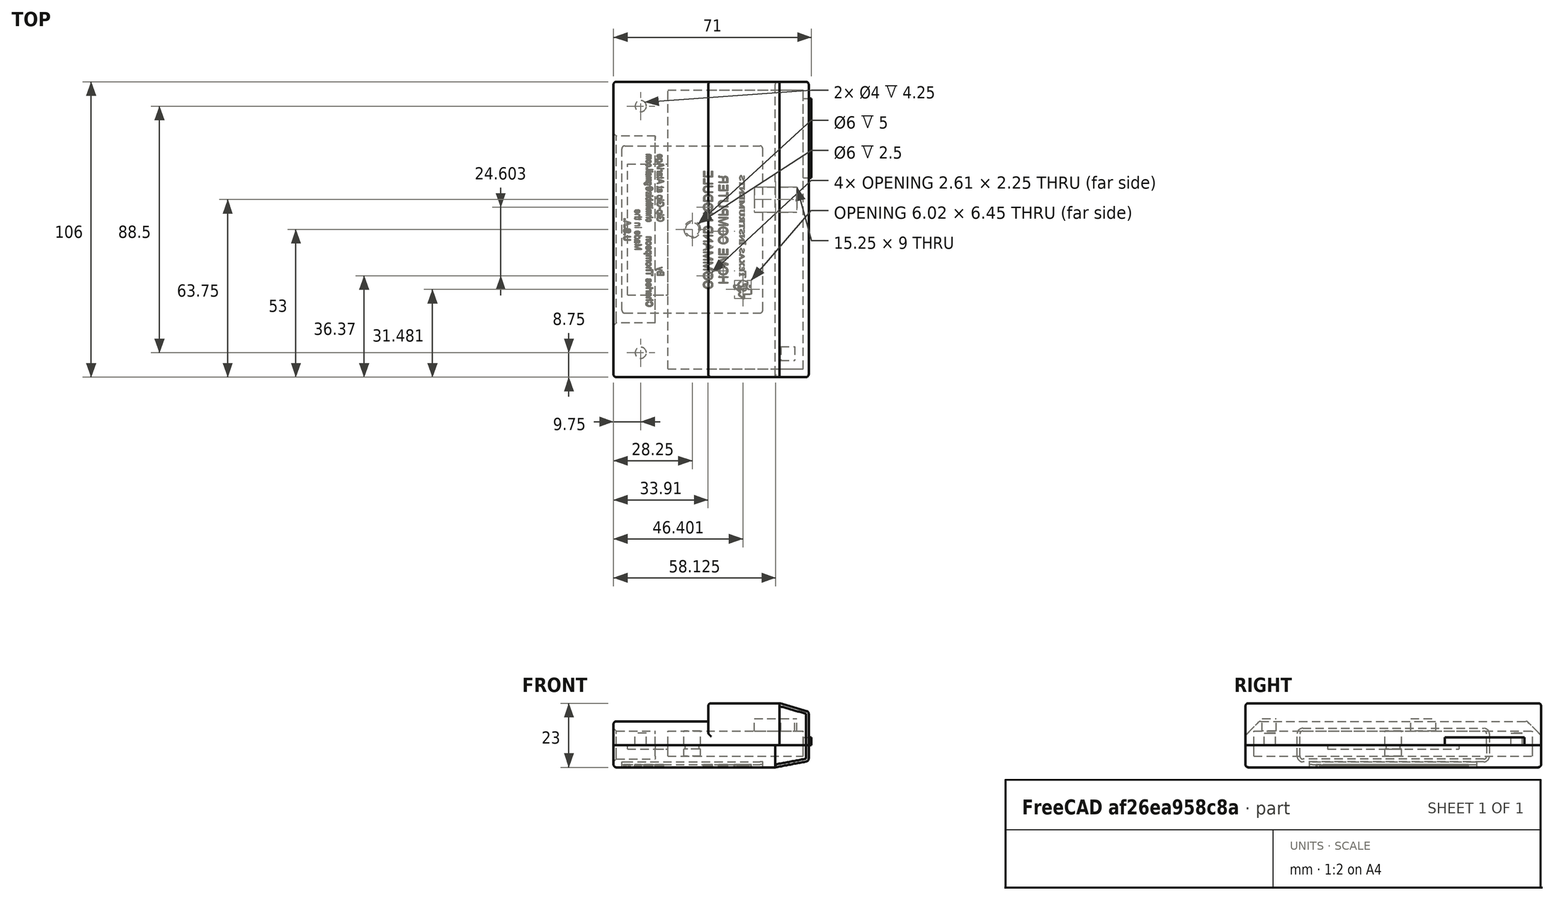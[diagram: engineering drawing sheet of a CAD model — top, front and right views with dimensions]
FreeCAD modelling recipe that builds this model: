
FCSTD DOCUMENT  (FreeCAD 0.17R11732 (Git))
Label: alcart
License: CC-BY 3.0
LicenseURL: http://creativecommons.org/licenses/by/3.0/
objects: Part::Feature×157, Part::Extrusion×119, Part::Cut×45, Part::MultiFuse×15, Part::Box×11, Part::Fillet×8, Part::Cylinder×5, Part::Chamfer×3, App::DocumentObjectGroup×3
note: 363 computed .brp shape members not serialized (recipe doc carries the construction recipe); baked Part::Feature solids carry a one-line shape summary decoded from their .brp

FEATURE [Part::Box] Box  label="fg_corepcb"
  AttacherType = Attacher::AttachEngine3D
  Height = 1.5
  Length = 48.5
  Placement = pos=(14.5,0,0) rot=(0,0,1;0rad)
  Width = 100
FEATURE [Part::Box] Box001  label="fg_connector"
  AttacherType = Attacher::AttachEngine3D
  Height = 1.5
  Length = 14.5
  Placement = pos=(0,26.5,0) rot=(0,0,1;0rad)
  Width = 47
FEATURE [Part::Box] Box002  label="fg_sdport"
  AttacherType = Attacher::AttachEngine3D
  Height = 2.75
  Length = 29
  Placement = pos=(37,68.5,1.5) rot=(0,0,1;0rad)
  Width = 28.5
FEATURE [Part::Box] Box004  label="fg_led"
  AttacherType = Attacher::AttachEngine3D
  Height = 9.5
  Length = 5
  Placement = pos=(55,3,1.5) rot=(0,0,1;0rad)
  Width = 5
FEATURE [Part::Box] Box003  label="fg_proginterface"
  AttacherType = Attacher::AttachEngine3D
  Height = 9.5
  Length = 15.25
  Placement = pos=(45.5,56.25,1.5) rot=(0,0,1;0rad)
  Width = 9
FEATURE [Part::Box] Box005  label="fg_componentarea"
  AttacherType = Attacher::AttachEngine3D
  Height = 9
  Length = 48.5
  Placement = pos=(14.5,0,-2.5) rot=(0,0,1;0rad)
  Width = 100
FEATURE [Part::Cylinder] Cylinder  label="fg_mounthole"
  Angle = 360
  AttacherType = Attacher::AttachEngine3D
  Height = 10
  Placement = pos=(23.25,50,-3) rot=(0,0,1;0rad)
  Radius = 2.5
FEATURE [Part::MultiFuse] Fusion  label="fg_mainboard"
  Shapes = -> [Box,Box005]
FEATURE [Part::Cut] Cut  label="fg_board/w/hole"
  Base = -> Fusion
  Tool = -> Cylinder
FEATURE [Part::Cylinder] Cylinder001  label="fg_mountrest1"
  Angle = 360
  AttacherType = Attacher::AttachEngine3D
  Height = 10
  Placement = pos=(23.25,50,1.5) rot=(0,0,1;0rad)
  Radius = 3
FEATURE [Part::Cut] Cut001  label="fg_board/w/rest1"
  Base = -> Cut
  Tool = -> Cylinder001
FEATURE [Part::Cylinder] Cylinder002  label="fg_mountrest2"
  Angle = 360
  AttacherType = Attacher::AttachEngine3D
  Height = 10
  Placement = pos=(23.25,50,-10) rot=(0,0,1;0rad)
  Radius = 3
FEATURE [Part::Cut] Cut002  label="fg_board/w/rest2"
  Base = -> Cut001
  Tool = -> Cylinder002
FEATURE [Part::Box] Box006  label="top_core"
  AttacherType = Attacher::AttachEngine3D
  Height = 8.5
  Length = 34
  Placement = pos=(-5,-3,1.5) rot=(0,0,1;0rad)
  Width = 106
FEATURE [Part::MultiFuse] Fusion001  label="fg_cutout1"
  Shapes = -> [Box001,Box002,Box004,Box003,Cut002]
FEATURE [Part::Box] Box007  label="top_head"
  AttacherType = Attacher::AttachEngine3D
  Height = 15
  Length = 25.5
  Placement = pos=(29,-3,1.5) rot=(0,0,1;0rad)
  Width = 106
FEATURE [Part::Chamfer] Chamfer  label="top_core_chamfer"
  Base = -> Box006
  Edges = 2 edges r=5: [Edge10,Edge12]
FEATURE [Part::MultiFuse] Fusion002
  Shapes = -> [Chamfer,Box007]
FEATURE [Part::Fillet] Fillet  label="top_fillets1"
  Base = -> Fusion002
  Edges = 5 edges r=1: [Edge7,Edge8,Edge9,Edge10,Edge13]
FEATURE [Part::Fillet] Fillet001  label="top_fillets_core&head"
  Base = -> Fillet
  Edges = 9 edges r=1: [Edge27,Edge28,Edge30,Edge31,Edge41,Edge42,Edge44,Edge45,Edge48]
FEATURE [Part::Feature] Solid  label="top_face"
  shape: bbox 10.5 x 106 x 15 mm, 6 faces (baked)
FEATURE [Part::Fillet] Fillet002  label="top_fillets_face"
  Base = -> Solid
  Edges = 5 edges r=1: [Edge8,Edge9,Edge10,Edge11,Edge12]
FEATURE [Part::MultiFuse] Fusion004  label="fg_complete"
  Shapes = -> [Box001,Box002,Box004,Box003,Cut002]
FEATURE [App::DocumentObjectGroup] Group  label="fg"
  Group = -> [Box,Box001,Box002,Box004,Box003,Box005,Cylinder,Fusion,Cut,Cylinder001,Cut001,Cut002,Fusion001,Fusion004]
FEATURE [Part::MultiFuse] Fusion003  label="top_complete"
  Shapes = -> [Fillet002,Fillet001]
FEATURE [Part::Cut] Cut003  label="top_cut1"
  Base = -> Fusion003
  Tool = -> Fusion001
FEATURE [Part::Box] Box008  label="bottom_core"
  AttacherType = Attacher::AttachEngine3D
  Height = 8
  Length = 58
  Placement = pos=(-5,-3,-6.5) rot=(0,0,1;0rad)
  Width = 106
FEATURE [Part::Feature] Solid001  label="bottom_chin"
  shape: bbox 12 x 106 x 8 mm, 6 faces (baked)
FEATURE [Part::Box] Box009  label="bottom_text_area"
  AttacherType = Attacher::AttachEngine3D
  Height = 1
  Length = 50.5
  Placement = pos=(-2,20,-6.5) rot=(0,0,1;0rad)
  Width = 60
FEATURE [Part::Fillet] Fillet003
  Base = -> Box009
  Edges = 4 edges r=1: [Edge1,Edge3,Edge5,Edge7]
FEATURE [Part::MultiFuse] Fusion005  label="bottom_w/o_fillets"
  Shapes = -> [Box008,Solid001]
FEATURE [Part::Fillet] Fillet004  label="bottom_complete"
  Base = -> Fusion005
  Edges = 10 edges r=1: [Edge1,Edge3,Edge4,Edge5,Edge10,Edge13,Edge15,Edge18,Edge19,Edge20]
FEATURE [Part::MultiFuse] Fusion006  label="fg_cutout2"
  Shapes = -> [Box001,Box002,Box004,Box003,Cut002]
FEATURE [Part::Cut] Cut004  label="bottom_cut1"
  Base = -> Fillet004
  Tool = -> Fusion006
FEATURE [Part::Box] Box010  label="Cube"
  AttacherType = Attacher::AttachEngine3D
  Height = 10
  Length = 15
  Placement = pos=(-5,16.5,-3.5) rot=(0,0,1;0rad)
  Width = 67
FEATURE [Part::Fillet] Fillet005  label="connector_cutout"
  Base = -> Box010
  Edges = 4 edges r=1: [Edge9,Edge10,Edge11,Edge12]
FEATURE [Part::Cut] Cut005  label="bottom_connector_cut"
  Base = -> Cut004
  Tool = -> Fillet005
FEATURE [Part::Fillet] Fillet006  label="connector_cutout2"
  Base = -> Box010
  Edges = 4 edges r=1: [Edge9,Edge10,Edge11,Edge12]
FEATURE [Part::Cut] Cut006  label="top_connector_cut"
  Base = -> Cut003
  Tool = -> Fillet006
FEATURE [Part::Cylinder] Cylinder003  label="index_1"
  Angle = 360
  AttacherType = Attacher::AttachEngine3D
  Height = 4.25
  Placement = pos=(0,5.75,1.5) rot=(0,0,1;0rad)
  Radius = 2
FEATURE [Part::Cylinder] Cylinder004  label="index_2"
  Angle = 360
  AttacherType = Attacher::AttachEngine3D
  Height = 4.25
  Placement = pos=(0,94.25,1.5) rot=(0,0,1;0rad)
  Radius = 2
FEATURE [Part::MultiFuse] Fusion007  label="index"
  Placement = pos=(4.75,0,0) rot=(0,0,1;0rad)
  Shapes = -> [Cylinder003,Cylinder004]
FEATURE [Part::MultiFuse] Fusion008  label="bottom_w_index"
  Shapes = -> [Cut005,Fusion007]
FEATURE [Part::MultiFuse] Fusion009  label="bottom_cutout"
  Shapes = -> [Cut005,Fusion007]
FEATURE [Part::Cut] Cut007  label="top_index_cutout"
  Base = -> Cut006
  Tool = -> Fusion009
FEATURE [Part::Feature] Face
  shape: bbox 6.877 x 6.384 x 2e-07 mm, 1 faces, 0 solids (baked)
FEATURE [Part::Feature] Face001
  shape: bbox 6.529 x 6.02 x 2e-07 mm, 1 faces, 0 solids (baked)
FEATURE [Part::Cut] Cut008
  Base = -> Face
  Tool = -> Face001
FEATURE [Part::Feature] Face002
  shape: bbox 1.264 x 2.322 x 2e-07 mm, 1 faces, 0 solids (baked)
FEATURE [Part::Feature] Face003
  shape: bbox 0.9803 x 2.192 x 2e-07 mm, 1 faces, 0 solids (baked)
FEATURE [Part::Cut] Cut009
  Base = -> Face002
  Tool = -> Face003
FEATURE [Part::Feature] Face004
  shape: bbox 0.6141 x 0.6141 x 2e-07 mm, 1 faces, 0 solids (baked)
FEATURE [Part::Feature] Face005
  shape: bbox 2.15 x 2.25 x 2.119e-07 mm, 1 faces, 0 solids (baked)
FEATURE [Part::Feature] Face006
  shape: bbox 1.67 x 1.637 x 2.385e-07 mm, 1 faces, 0 solids (baked)
FEATURE [Part::Feature] Face007
  shape: bbox 2.213 x 1.637 x 2.385e-07 mm, 1 faces, 0 solids (baked)
FEATURE [Part::Feature] Face008
  shape: bbox 2.213 x 1.711 x 2.385e-07 mm, 1 faces, 0 solids (baked)
FEATURE [Part::Feature] Face009
  shape: bbox 0.641 x 0.6678 x 2.385e-07 mm, 1 faces, 0 solids (baked)
FEATURE [Part::Cut] Cut010
  Base = -> Face008
  Tool = -> Face009
FEATURE [Part::Feature] Face010
  shape: bbox 1.419 x 1.715 x 2.385e-07 mm, 1 faces, 0 solids (baked)
FEATURE [Part::Feature] Face011
  shape: bbox 0.75 x 2.25 x 2.07e-07 mm, 1 faces, 0 solids (baked)
FEATURE [Part::Feature] Face012
  shape: bbox 2.382 x 1.71 x 2.417e-07 mm, 1 faces, 0 solids (baked)
FEATURE [Part::Feature] Face013
  shape: bbox 1.487 x 1.75 x 2.417e-07 mm, 1 faces, 0 solids (baked)
FEATURE [Part::Feature] Face014
  shape: bbox 2.078 x 1.671 x 2.417e-07 mm, 1 faces, 0 solids (baked)
FEATURE [Part::Feature] Face015
  shape: bbox 0.8461 x 0.693 x 2.417e-07 mm, 1 faces, 0 solids (baked)
FEATURE [Part::Feature] Face016
  shape: bbox 2.126 x 1.729 x 2.417e-07 mm, 1 faces, 0 solids (baked)
FEATURE [Part::Cut] Cut011
  Base = -> Face016
  Tool = -> Face015
FEATURE [Part::Feature] Face017
  shape: bbox 2.372 x 1.71 x 2.417e-07 mm, 1 faces, 0 solids (baked)
FEATURE [Part::Feature] Face018
  shape: bbox 2.924 x 1.67 x 2.417e-07 mm, 1 faces, 0 solids (baked)
FEATURE [Part::Feature] Face019
  shape: bbox 1.75 x 1.67 x 2.417e-07 mm, 1 faces, 0 solids (baked)
FEATURE [Part::Feature] Face020
  shape: bbox 2.382 x 1.71 x 2.417e-07 mm, 1 faces, 0 solids (baked)
FEATURE [Part::Feature] Face021
  shape: bbox 2.078 x 1.671 x 2.417e-07 mm, 1 faces, 0 solids (baked)
FEATURE [Part::Feature] Face022
  shape: bbox 1.487 x 1.75 x 2.417e-07 mm, 1 faces, 0 solids (baked)
FEATURE [Part::Extrusion] Extrude
  Base = -> Cut008
  Dir = (0,0,-1)
  DirMode = 2
  FaceMakerClass = Part::FaceMakerBullseye
  LengthFwd = 1
  LengthRev = 0
  Solid = false
  Symmetric = false
FEATURE [Part::Extrusion] Extrude001
  Base = -> Cut009
  Dir = (0,0,-1)
  DirMode = 2
  FaceMakerClass = Part::FaceMakerBullseye
  LengthFwd = 1
  LengthRev = 0
  Solid = false
  Symmetric = false
FEATURE [Part::Extrusion] Extrude002
  Base = -> Face004
  Dir = (0,0,1)
  DirMode = 2
  FaceMakerClass = Part::FaceMakerBullseye
  LengthFwd = -1
  LengthRev = 0
  Solid = false
  Symmetric = false
FEATURE [Part::Extrusion] Extrude003
  Base = -> Face005
  Dir = (0,0,1)
  DirMode = 2
  FaceMakerClass = Part::FaceMakerBullseye
  LengthFwd = -1
  LengthRev = 0
  Solid = false
  Symmetric = false
FEATURE [Part::Extrusion] Extrude004
  Base = -> Face006
  Dir = (0,0,1)
  DirMode = 2
  FaceMakerClass = Part::FaceMakerBullseye
  LengthFwd = -1
  LengthRev = 0
  Solid = false
  Symmetric = false
FEATURE [Part::Extrusion] Extrude005
  Base = -> Face007
  Dir = (0,0,1)
  DirMode = 2
  FaceMakerClass = Part::FaceMakerBullseye
  LengthFwd = -1
  LengthRev = 0
  Solid = false
  Symmetric = false
FEATURE [Part::Extrusion] Extrude006
  Base = -> Cut010
  Dir = (0,0,1)
  DirMode = 2
  FaceMakerClass = Part::FaceMakerBullseye
  LengthFwd = -1
  LengthRev = 0
  Solid = false
  Symmetric = false
FEATURE [Part::Extrusion] Extrude007
  Base = -> Face010
  Dir = (0,0,1)
  DirMode = 2
  FaceMakerClass = Part::FaceMakerBullseye
  LengthFwd = -1
  LengthRev = 0
  Solid = false
  Symmetric = false
FEATURE [Part::Extrusion] Extrude008
  Base = -> Face011
  Dir = (0,0,1)
  DirMode = 2
  FaceMakerClass = Part::FaceMakerBullseye
  LengthFwd = -1
  LengthRev = 0
  Solid = false
  Symmetric = false
FEATURE [Part::Extrusion] Extrude009
  Base = -> Face012
  Dir = (0,0,1)
  DirMode = 2
  FaceMakerClass = Part::FaceMakerBullseye
  LengthFwd = -1
  LengthRev = 0
  Solid = false
  Symmetric = false
FEATURE [Part::Extrusion] Extrude010
  Base = -> Face013
  Dir = (0,0,1)
  DirMode = 2
  FaceMakerClass = Part::FaceMakerBullseye
  LengthFwd = -1
  LengthRev = 0
  Solid = false
  Symmetric = false
FEATURE [Part::Extrusion] Extrude011
  Base = -> Face014
  Dir = (0,0,1)
  DirMode = 2
  FaceMakerClass = Part::FaceMakerBullseye
  LengthFwd = -1
  LengthRev = 0
  Solid = false
  Symmetric = false
FEATURE [Part::Extrusion] Extrude012
  Base = -> Cut011
  Dir = (0,0,1)
  DirMode = 2
  FaceMakerClass = Part::FaceMakerBullseye
  LengthFwd = -1
  LengthRev = 0
  Solid = false
  Symmetric = false
FEATURE [Part::Extrusion] Extrude013
  Base = -> Face017
  Dir = (0,0,-1)
  DirMode = 2
  FaceMakerClass = Part::FaceMakerBullseye
  LengthFwd = 1
  LengthRev = 0
  Solid = false
  Symmetric = false
FEATURE [Part::Extrusion] Extrude014
  Base = -> Face018
  Dir = (0,0,-1)
  DirMode = 2
  FaceMakerClass = Part::FaceMakerBullseye
  LengthFwd = 1
  LengthRev = 0
  Solid = false
  Symmetric = false
FEATURE [Part::Extrusion] Extrude015
  Base = -> Face019
  Dir = (0,0,1)
  DirMode = 2
  FaceMakerClass = Part::FaceMakerBullseye
  LengthFwd = -1
  LengthRev = 0
  Solid = false
  Symmetric = false
FEATURE [Part::Extrusion] Extrude016
  Base = -> Face020
  Dir = (0,0,1)
  DirMode = 2
  FaceMakerClass = Part::FaceMakerBullseye
  LengthFwd = -1
  LengthRev = 0
  Solid = false
  Symmetric = false
FEATURE [Part::Extrusion] Extrude017
  Base = -> Face021
  Dir = (0,0,1)
  DirMode = 2
  FaceMakerClass = Part::FaceMakerBullseye
  LengthFwd = -1
  LengthRev = 0
  Solid = false
  Symmetric = false
FEATURE [Part::Extrusion] Extrude018
  Base = -> Face022
  Dir = (0,0,1)
  DirMode = 2
  FaceMakerClass = Part::FaceMakerBullseye
  LengthFwd = -1
  LengthRev = 0
  Solid = false
  Symmetric = false
FEATURE [Part::MultiFuse] Fusion010  label="texas_instruments"
  Placement = pos=(44.5,25,-6.5) rot=(0.707107,0.707107,0;3.14159rad)
  Shapes = -> [Extrude018,Extrude,Extrude002,Extrude006,Extrude003,Extrude001,Extrude004,Extrude005,Extrude007,Extrude009,Extrude008,Extrude010,Extrude014,Extrude012,Extrude011,Extrude015,Extrude013,Extrude017,Extrude016]
FEATURE [Part::Cut] Cut012  label="bottom_w_textbox"
  Base = -> Fusion008
  Tool = -> Fillet003
FEATURE [Part::Feature] Face023
  shape: bbox 2.434 x 3.167 x 2.001e-07 mm, 1 faces, 0 solids (baked)
FEATURE [Part::Feature] Face024
  shape: bbox 3.055 x 3.319 x 2.001e-07 mm, 1 faces, 0 solids (baked)
FEATURE [Part::Feature] Face025
  shape: bbox 2.248 x 2.607 x 2.001e-07 mm, 1 faces, 0 solids (baked)
FEATURE [Part::Cut] Cut013
  Base = -> Face024
  Tool = -> Face025
FEATURE [Part::Feature] Face026
  shape: bbox 2.977 x 3.167 x 2.001e-07 mm, 1 faces, 0 solids (baked)
FEATURE [Part::Feature] Face027
  shape: bbox 2.269 x 3.167 x 2.001e-07 mm, 1 faces, 0 solids (baked)
FEATURE [Part::Feature] Face028
  shape: bbox 2.729 x 3.319 x 2.001e-07 mm, 1 faces, 0 solids (baked)
FEATURE [Part::Feature] Face029
  shape: bbox 3.055 x 3.319 x 2.001e-07 mm, 1 faces, 0 solids (baked)
FEATURE [Part::Feature] Face030
  shape: bbox 2.248 x 2.607 x 2.001e-07 mm, 1 faces, 0 solids (baked)
FEATURE [Part::Cut] Cut014
  Base = -> Face029
  Tool = -> Face030
FEATURE [Part::Feature] Face031
  shape: bbox 2.977 x 3.167 x 2.001e-07 mm, 1 faces, 0 solids (baked)
FEATURE [Part::Feature] Face032
  shape: bbox 2.282 x 3.167 x 2.001e-07 mm, 1 faces, 0 solids (baked)
FEATURE [Part::Feature] Face033
  shape: bbox 1.458 x 1.112 x 2.001e-07 mm, 1 faces, 0 solids (baked)
FEATURE [Part::Cut] Cut015
  Base = -> Face032
  Tool = -> Face033
FEATURE [Part::Feature] Face034
  shape: bbox 2.43 x 3.267 x 2.001e-07 mm, 1 faces, 0 solids (baked)
FEATURE [Part::Feature] Face035
  shape: bbox 2.482 x 3.167 x 2.001e-07 mm, 1 faces, 0 solids (baked)
FEATURE [Part::Feature] Face036
  shape: bbox 2.269 x 3.167 x 2.001e-07 mm, 1 faces, 0 solids (baked)
FEATURE [Part::Feature] Face037
  shape: bbox 2.543 x 3.167 x 2.001e-07 mm, 1 faces, 0 solids (baked)
FEATURE [Part::Feature] Face038
  shape: bbox 1.597 x 1.09 x 2.001e-07 mm, 1 faces, 0 solids (baked)
FEATURE [Part::Cut] Cut016
  Base = -> Face037
  Tool = -> Face038
FEATURE [Part::Feature] Face039
  shape: bbox 2.729 x 3.319 x 2.001e-07 mm, 1 faces, 0 solids (baked)
FEATURE [Part::Feature] Face040
  shape: bbox 3.055 x 3.319 x 2.001e-07 mm, 1 faces, 0 solids (baked)
FEATURE [Part::Feature] Face041
  shape: bbox 2.248 x 2.607 x 2.001e-07 mm, 1 faces, 0 solids (baked)
FEATURE [Part::Cut] Cut017
  Base = -> Face040
  Tool = -> Face041
FEATURE [Part::Feature] Face042
  shape: bbox 2.977 x 3.167 x 2.001e-07 mm, 1 faces, 0 solids (baked)
FEATURE [Part::Feature] Face043
  shape: bbox 2.977 x 3.167 x 2.001e-07 mm, 1 faces, 0 solids (baked)
FEATURE [Part::Feature] Face044
  shape: bbox 1.007 x 1.442 x 2.001e-07 mm, 1 faces, 0 solids (baked)
FEATURE [Part::Feature] Face045
  shape: bbox 2.76 x 3.167 x 2.001e-07 mm, 1 faces, 0 solids (baked)
FEATURE [Part::Cut] Cut018
  Base = -> Face045
  Tool = -> Face044
FEATURE [Part::Feature] Face046
  shape: bbox 2.473 x 3.167 x 2.001e-07 mm, 1 faces, 0 solids (baked)
FEATURE [Part::Feature] Face047
  shape: bbox 2.508 x 3.167 x 2.001e-07 mm, 1 faces, 0 solids (baked)
FEATURE [Part::Feature] Face048
  shape: bbox 1.701 x 2.455 x 2.001e-07 mm, 1 faces, 0 solids (baked)
FEATURE [Part::Cut] Cut019
  Base = -> Face047
  Tool = -> Face048
FEATURE [Part::Feature] Face049
  shape: bbox 2.977 x 3.167 x 2.001e-07 mm, 1 faces, 0 solids (baked)
FEATURE [Part::Feature] Face050
  shape: bbox 3.055 x 3.319 x 2.001e-07 mm, 1 faces, 0 solids (baked)
FEATURE [Part::Feature] Face051
  shape: bbox 2.248 x 2.607 x 2.001e-07 mm, 1 faces, 0 solids (baked)
FEATURE [Part::Cut] Cut020
  Base = -> Face050
  Tool = -> Face051
FEATURE [Part::Feature] Face052
  shape: bbox 2.508 x 3.167 x 2.001e-07 mm, 1 faces, 0 solids (baked)
FEATURE [Part::Feature] Face053
  shape: bbox 1.701 x 2.455 x 2.001e-07 mm, 1 faces, 0 solids (baked)
FEATURE [Part::Cut] Cut021
  Base = -> Face052
  Tool = -> Face053
FEATURE [Part::Feature] Face054
  shape: bbox 2.43 x 3.267 x 2.001e-07 mm, 1 faces, 0 solids (baked)
FEATURE [Part::Feature] Face055
  shape: bbox 1.966 x 3.167 x 2.001e-07 mm, 1 faces, 0 solids (baked)
FEATURE [Part::Feature] Face056
  shape: bbox 2.269 x 3.167 x 2.001e-07 mm, 1 faces, 0 solids (baked)
FEATURE [Part::Extrusion] Extrude019
  Base = -> Face023
  Dir = (0,0,-1)
  DirMode = 2
  FaceMakerClass = Part::FaceMakerBullseye
  LengthFwd = 1
  LengthRev = 0
  Solid = true
  Symmetric = false
FEATURE [Part::Extrusion] Extrude020
  Base = -> Cut013
  Dir = (0,0,-1)
  DirMode = 2
  FaceMakerClass = Part::FaceMakerBullseye
  LengthFwd = 1
  LengthRev = 0
  Solid = true
  Symmetric = false
FEATURE [Part::Extrusion] Extrude021
  Base = -> Face026
  Dir = (0,0,1)
  DirMode = 2
  FaceMakerClass = Part::FaceMakerBullseye
  LengthFwd = -1
  LengthRev = 0
  Solid = true
  Symmetric = false
FEATURE [Part::Extrusion] Extrude022
  Base = -> Face027
  Dir = (0,0,-1)
  DirMode = 2
  FaceMakerClass = Part::FaceMakerBullseye
  LengthFwd = 1
  LengthRev = 0
  Solid = true
  Symmetric = false
FEATURE [Part::Extrusion] Extrude023
  Base = -> Face028
  Dir = (0,0,-1)
  DirMode = 2
  FaceMakerClass = Part::FaceMakerBullseye
  LengthFwd = 1
  LengthRev = 0
  Solid = true
  Symmetric = false
FEATURE [Part::Extrusion] Extrude024
  Base = -> Cut014
  Dir = (0,0,-1)
  DirMode = 2
  FaceMakerClass = Part::FaceMakerBullseye
  LengthFwd = 1
  LengthRev = 0
  Solid = true
  Symmetric = false
FEATURE [Part::Extrusion] Extrude025
  Base = -> Face031
  Dir = (0,0,1)
  DirMode = 2
  FaceMakerClass = Part::FaceMakerBullseye
  LengthFwd = -1
  LengthRev = 0
  Solid = true
  Symmetric = false
FEATURE [Part::Extrusion] Extrude026
  Base = -> Cut015
  Dir = (0,0,-1)
  DirMode = 2
  FaceMakerClass = Part::FaceMakerBullseye
  LengthFwd = 1
  LengthRev = 0
  Solid = true
  Symmetric = false
FEATURE [Part::Extrusion] Extrude027
  Base = -> Face034
  Dir = (0,0,1)
  DirMode = 2
  FaceMakerClass = Part::FaceMakerBullseye
  LengthFwd = -1
  LengthRev = 0
  Solid = true
  Symmetric = false
FEATURE [Part::Extrusion] Extrude028
  Base = -> Face035
  Dir = (0,0,-1)
  DirMode = 2
  FaceMakerClass = Part::FaceMakerBullseye
  LengthFwd = 1
  LengthRev = 0
  Solid = true
  Symmetric = false
FEATURE [Part::Extrusion] Extrude029
  Base = -> Face036
  Dir = (0,0,-1)
  DirMode = 2
  FaceMakerClass = Part::FaceMakerBullseye
  LengthFwd = 1
  LengthRev = 0
  Solid = true
  Symmetric = false
FEATURE [Part::Extrusion] Extrude030
  Base = -> Cut016
  Dir = (0,0,1)
  DirMode = 2
  FaceMakerClass = Part::FaceMakerBullseye
  LengthFwd = -1
  LengthRev = 0
  Solid = true
  Symmetric = false
FEATURE [Part::Extrusion] Extrude031
  Base = -> Face039
  Dir = (0,0,-1)
  DirMode = 2
  FaceMakerClass = Part::FaceMakerBullseye
  LengthFwd = 1
  LengthRev = 0
  Solid = true
  Symmetric = false
FEATURE [Part::Extrusion] Extrude032
  Base = -> Cut017
  Dir = (0,0,-1)
  DirMode = 2
  FaceMakerClass = Part::FaceMakerBullseye
  LengthFwd = 1
  LengthRev = 0
  Solid = true
  Symmetric = false
FEATURE [Part::Extrusion] Extrude033
  Base = -> Face042
  Dir = (0,0,1)
  DirMode = 2
  FaceMakerClass = Part::FaceMakerBullseye
  LengthFwd = -1
  LengthRev = 0
  Solid = true
  Symmetric = false
FEATURE [Part::Extrusion] Extrude034
  Base = -> Face043
  Dir = (0,0,1)
  DirMode = 2
  FaceMakerClass = Part::FaceMakerBullseye
  LengthFwd = -1
  LengthRev = 0
  Solid = true
  Symmetric = false
FEATURE [Part::Extrusion] Extrude035
  Base = -> Cut018
  Dir = (0,0,-1)
  DirMode = 2
  FaceMakerClass = Part::FaceMakerBullseye
  LengthFwd = 1
  LengthRev = 0
  Solid = true
  Symmetric = false
FEATURE [Part::Extrusion] Extrude036
  Base = -> Face046
  Dir = (0,0,-1)
  DirMode = 2
  FaceMakerClass = Part::FaceMakerBullseye
  LengthFwd = 1
  LengthRev = 0
  Solid = true
  Symmetric = false
FEATURE [Part::Extrusion] Extrude037
  Base = -> Cut019
  Dir = (0,0,-1)
  DirMode = 2
  FaceMakerClass = Part::FaceMakerBullseye
  LengthFwd = 1
  LengthRev = 0
  Solid = true
  Symmetric = false
FEATURE [Part::Extrusion] Extrude038
  Base = -> Face049
  Dir = (0,0,1)
  DirMode = 2
  FaceMakerClass = Part::FaceMakerBullseye
  LengthFwd = -1
  LengthRev = 0
  Solid = true
  Symmetric = false
FEATURE [Part::Extrusion] Extrude039
  Base = -> Cut020
  Dir = (0,0,-1)
  DirMode = 2
  FaceMakerClass = Part::FaceMakerBullseye
  LengthFwd = 1
  LengthRev = 0
  Solid = true
  Symmetric = false
FEATURE [Part::Extrusion] Extrude040
  Base = -> Cut021
  Dir = (0,0,-1)
  DirMode = 2
  FaceMakerClass = Part::FaceMakerBullseye
  LengthFwd = 1
  LengthRev = 0
  Solid = true
  Symmetric = false
FEATURE [Part::Extrusion] Extrude041
  Base = -> Face054
  Dir = (0,0,1)
  DirMode = 2
  FaceMakerClass = Part::FaceMakerBullseye
  LengthFwd = -1
  LengthRev = 0
  Solid = true
  Symmetric = false
FEATURE [Part::Extrusion] Extrude042
  Base = -> Face056
  Dir = (0,0,-1)
  DirMode = 2
  FaceMakerClass = Part::FaceMakerBullseye
  LengthFwd = 1
  LengthRev = 0
  Solid = true
  Symmetric = false
FEATURE [Part::Extrusion] Extrude043
  Base = -> Face055
  Dir = (0,0,-1)
  DirMode = 2
  FaceMakerClass = Part::FaceMakerBullseye
  LengthFwd = 1
  LengthRev = 0
  Solid = true
  Symmetric = false
FEATURE [Part::MultiFuse] Fusion011  label="command_module"
  Placement = pos=(36,28.75,-6.5) rot=(0.707107,0.707107,0;3.14159rad)
  Shapes = -> [Extrude031,Extrude019,Extrude020,Extrude021,Extrude022,Extrude037,Extrude023,Extrude025,Extrude024,Extrude026,Extrude027,Extrude028,Extrude032,Extrude034,Extrude029,Extrude030,Extrude033,Extrude035,Extrude036,Extrude038,Extrude039,Extrude040,Extrude041,Extrude042,Extrude043]
FEATURE [Part::Feature] Face057
  shape: bbox 1.929 x 2.309 x 2e-07 mm, 1 faces, 0 solids (baked)
FEATURE [Part::Feature] Face058
  shape: bbox 1.386 x 1.78 x 2e-07 mm, 1 faces, 0 solids (baked)
FEATURE [Part::Feature] Face059
  shape: bbox 0.731 x 0.6621 x 2e-07 mm, 1 faces, 0 solids (baked)
FEATURE [Part::Cut] Cut022
  Base = -> Face058
  Tool = -> Face059
FEATURE [Part::Feature] Face060
  shape: bbox 1.319 x 2.382 x 2e-07 mm, 1 faces, 0 solids (baked)
FEATURE [Part::Feature] Face061
  shape: bbox 0.8407 x 1.286 x 2e-07 mm, 1 faces, 0 solids (baked)
FEATURE [Part::Cut] Cut023
  Base = -> Face060
  Tool = -> Face061
FEATURE [Part::Feature] Face062
  shape: bbox 1.33 x 1.78 x 2e-07 mm, 1 faces, 0 solids (baked)
FEATURE [Part::Feature] Face063
  shape: bbox 0.8295 x 0.5069 x 2e-07 mm, 1 faces, 0 solids (baked)
FEATURE [Part::Cut] Cut024
  Base = -> Face062
  Tool = -> Face063
FEATURE [Part::Feature] Face064
  shape: bbox 0.2334 x 1.66 x 2e-07 mm, 1 faces, 0 solids (baked)
FEATURE [Part::Feature] Face065
  shape: bbox 0.2362 x 0.3326 x 2e-07 mm, 1 faces, 0 solids (baked)
FEATURE [Part::Feature] Face066
  shape: bbox 1.172 x 1.707 x 2e-07 mm, 1 faces, 0 solids (baked)
FEATURE [Part::Feature] Face067
  shape: bbox 0.6748 x 2.189 x 2e-07 mm, 1 faces, 0 solids (baked)
FEATURE [Part::Feature] Face068
  shape: bbox 1.17 x 2.309 x 2e-07 mm, 1 faces, 0 solids (baked)
FEATURE [Part::Feature] Face069
  shape: bbox 1.33 x 1.78 x 2e-07 mm, 1 faces, 0 solids (baked)
FEATURE [Part::Feature] Face070
  shape: bbox 0.8295 x 0.5069 x 2e-07 mm, 1 faces, 0 solids (baked)
FEATURE [Part::Cut] Cut025
  Base = -> Face069
  Tool = -> Face070
FEATURE [Part::Feature] Face071
  shape: bbox 1.625 x 2.382 x 2e-07 mm, 1 faces, 0 solids (baked)
FEATURE [Part::Feature] Face072
  shape: bbox 0.4218 x 0.4625 x 2e-07 mm, 1 faces, 0 solids (baked)
FEATURE [Part::Feature] Face073
  shape: bbox 1.69 x 2.42 x 2e-07 mm, 1 faces, 0 solids (baked)
FEATURE [Part::Feature] Face074
  shape: bbox 0.4218 x 0.4625 x 2e-07 mm, 1 faces, 0 solids (baked)
FEATURE [Part::Feature] Face075
  shape: bbox 1.904 x 2.309 x 2e-07 mm, 1 faces, 0 solids (baked)
FEATURE [Part::Feature] Face076
  shape: bbox 0.5342 x 0.9029 x 2e-07 mm, 1 faces, 0 solids (baked)
FEATURE [Part::Cut] Cut026
  Base = -> Face075
  Tool = -> Face076
FEATURE [Part::Feature] Face077
  shape: bbox 0.4218 x 0.4625 x 2e-07 mm, 1 faces, 0 solids (baked)
FEATURE [Part::Extrusion] Extrude044
  Base = -> Face057
  Dir = (0,0,1)
  DirMode = 2
  FaceMakerClass = Part::FaceMakerBullseye
  LengthFwd = -1
  LengthRev = 0
  Solid = true
  Symmetric = false
FEATURE [Part::Extrusion] Extrude045
  Base = -> Cut022
  Dir = (0,0,1)
  DirMode = 2
  FaceMakerClass = Part::FaceMakerBullseye
  LengthFwd = -1
  LengthRev = 0
  Solid = true
  Symmetric = false
FEATURE [Part::Extrusion] Extrude046
  Base = -> Cut023
  Dir = (0,0,-1)
  DirMode = 2
  FaceMakerClass = Part::FaceMakerBullseye
  LengthFwd = 1
  LengthRev = 0
  Solid = true
  Symmetric = false
FEATURE [Part::Extrusion] Extrude047
  Base = -> Cut024
  Dir = (0,0,-1)
  DirMode = 2
  FaceMakerClass = Part::FaceMakerBullseye
  LengthFwd = 1
  LengthRev = 0
  Solid = true
  Symmetric = false
FEATURE [Part::Extrusion] Extrude048
  Base = -> Face064
  Dir = (0,0,-1)
  DirMode = 2
  FaceMakerClass = Part::FaceMakerBullseye
  LengthFwd = 1
  LengthRev = 0
  Solid = true
  Symmetric = false
FEATURE [Part::Extrusion] Extrude049
  Base = -> Face065
  Dir = (0,0,-1)
  DirMode = 2
  FaceMakerClass = Part::FaceMakerBullseye
  LengthFwd = 1
  LengthRev = 0
  Solid = true
  Symmetric = false
FEATURE [Part::Extrusion] Extrude050
  Base = -> Face066
  Dir = (0,0,-1)
  DirMode = 2
  FaceMakerClass = Part::FaceMakerBullseye
  LengthFwd = 1
  LengthRev = 0
  Solid = true
  Symmetric = false
FEATURE [Part::Extrusion] Extrude051
  Base = -> Face067
  Dir = (0,0,1)
  DirMode = 2
  FaceMakerClass = Part::FaceMakerBullseye
  LengthFwd = -1
  LengthRev = 0
  Solid = true
  Symmetric = false
FEATURE [Part::Extrusion] Extrude052
  Base = -> Face068
  Dir = (0,0,-1)
  DirMode = 2
  FaceMakerClass = Part::FaceMakerBullseye
  LengthFwd = 1
  LengthRev = 0
  Solid = true
  Symmetric = false
FEATURE [Part::Extrusion] Extrude053
  Base = -> Cut025
  Dir = (0,0,-1)
  DirMode = 2
  FaceMakerClass = Part::FaceMakerBullseye
  LengthFwd = 1
  LengthRev = 0
  Solid = true
  Symmetric = false
FEATURE [Part::Extrusion] Extrude054
  Base = -> Face071
  Dir = (0,0,1)
  DirMode = 2
  FaceMakerClass = Part::FaceMakerBullseye
  LengthFwd = -1
  LengthRev = 0
  Solid = true
  Symmetric = false
FEATURE [Part::Extrusion] Extrude055
  Base = -> Face072
  Dir = (0,0,-1)
  DirMode = 2
  FaceMakerClass = Part::FaceMakerBullseye
  LengthFwd = 1
  LengthRev = 0
  Solid = true
  Symmetric = false
FEATURE [Part::Extrusion] Extrude056
  Base = -> Face074
  Dir = (0,0,-1)
  DirMode = 2
  FaceMakerClass = Part::FaceMakerBullseye
  LengthFwd = 1
  LengthRev = 0
  Solid = true
  Symmetric = false
FEATURE [Part::Extrusion] Extrude057
  Base = -> Face073
  Dir = (0,0,-1)
  DirMode = 2
  FaceMakerClass = Part::FaceMakerBullseye
  LengthFwd = 1
  LengthRev = 0
  Solid = true
  Symmetric = false
FEATURE [Part::Extrusion] Extrude058
  Base = -> Cut026
  Dir = (0,0,-1)
  DirMode = 2
  FaceMakerClass = Part::FaceMakerBullseye
  LengthFwd = 1
  LengthRev = 0
  Solid = true
  Symmetric = false
FEATURE [Part::Extrusion] Extrude059
  Base = -> Face077
  Dir = (0,0,-1)
  DirMode = 2
  FaceMakerClass = Part::FaceMakerBullseye
  LengthFwd = 1
  LengthRev = 0
  Solid = true
  Symmetric = false
FEATURE [Part::MultiFuse] Fusion012  label="origin"
  Placement = pos=(5,37,-6.5) rot=(0.707107,0.707107,0;3.14159rad)
  Shapes = -> [Extrude059,Extrude056,Extrude058,Extrude057,Extrude053,Extrude055,Extrude052,Extrude054,Extrude050,Extrude051,Extrude048,Extrude046,Extrude049,Extrude047,Extrude045,Extrude044]
FEATURE [Part::Feature] Subtraction
  shape: bbox 1.53 x 2.309 x 2e-07 mm, 1 faces, 0 solids (baked)
FEATURE [Part::Feature] Face078
  shape: bbox 1.288 x 2.351 x 2e-07 mm, 1 faces, 0 solids (baked)
FEATURE [Part::Feature] Face079
  shape: bbox 1.802 x 2.42 x 2e-07 mm, 1 faces, 0 solids (baked)
FEATURE [Part::Feature] Face080
  shape: bbox 1.333 x 2.309 x 2e-07 mm, 1 faces, 0 solids (baked)
FEATURE [Part::Feature] Face081
  shape: bbox 1.395 x 1.812 x 2e-07 mm, 1 faces, 0 solids (baked)
FEATURE [Part::Feature] Face082
  shape: bbox 0.5258 x 0.5227 x 2e-07 mm, 1 faces, 0 solids (baked)
FEATURE [Part::Cut] Cut027
  Base = -> Face081
  Tool = -> Face082
FEATURE [Part::Feature] Face083
  shape: bbox 0.8632 x 1.739 x 2e-07 mm, 1 faces, 0 solids (baked)
FEATURE [Part::Feature] Face084
  shape: bbox 0.3936 x 2.309 x 2e-07 mm, 1 faces, 0 solids (baked)
FEATURE [Part::Feature] Face085
  shape: bbox 1.414 x 1.812 x 2e-07 mm, 1 faces, 0 solids (baked)
FEATURE [Part::Feature] Face086
  shape: bbox 0.6045 x 0.3897 x 2e-07 mm, 1 faces, 0 solids (baked)
FEATURE [Part::Cut] Cut028
  Base = -> Face085
  Tool = -> Face086
FEATURE [Part::Feature] Face087
  shape: bbox 1.381 x 1.812 x 2e-07 mm, 1 faces, 0 solids (baked)
FEATURE [Part::Feature] Face088
  shape: bbox 1.642 x 2.309 x 2e-07 mm, 1 faces, 0 solids (baked)
FEATURE [Part::Feature] Face089
  shape: bbox 1.333 x 2.309 x 2e-07 mm, 1 faces, 0 solids (baked)
FEATURE [Part::Feature] Face090
  shape: bbox 1.501 x 1.812 x 2e-07 mm, 1 faces, 0 solids (baked)
FEATURE [Part::Feature] Face091
  shape: bbox 0.7142 x 1.096 x 2e-07 mm, 1 faces, 0 solids (baked)
FEATURE [Part::Cut] Cut029
  Base = -> Face090
  Tool = -> Face091
FEATURE [Part::Feature] Face092
  shape: bbox 2.148 x 1.739 x 2e-07 mm, 1 faces, 0 solids (baked)
FEATURE [Part::Feature] Face093
  shape: bbox 1.451 x 2.43 x 2e-07 mm, 1 faces, 0 solids (baked)
FEATURE [Part::Feature] Face094
  shape: bbox 0.6636 x 1.074 x 2e-07 mm, 1 faces, 0 solids (baked)
FEATURE [Part::Cut] Cut030
  Base = -> Face093
  Tool = -> Face094
FEATURE [Part::Feature] Face095
  shape: bbox 1.381 x 1.812 x 2e-07 mm, 1 faces, 0 solids (baked)
FEATURE [Part::Feature] Face096
  shape: bbox 1.501 x 1.812 x 2e-07 mm, 1 faces, 0 solids (baked)
FEATURE [Part::Feature] Face097
  shape: bbox 0.7142 x 1.096 x 2e-07 mm, 1 faces, 0 solids (baked)
FEATURE [Part::Cut] Cut031
  Base = -> Face096
  Tool = -> Face097
FEATURE [Part::Feature] Face098
  shape: bbox 1.358 x 1.739 x 2e-07 mm, 1 faces, 0 solids (baked)
FEATURE [Part::Extrusion] Extrude060
  Base = -> Subtraction
  Dir = (0,0,-1)
  DirMode = 2
  FaceMakerClass = Part::FaceMakerBullseye
  LengthFwd = 1
  LengthRev = 0
  Solid = true
  Symmetric = false
FEATURE [Part::Extrusion] Extrude061
  Base = -> Face078
  Dir = (0,0,1)
  DirMode = 2
  FaceMakerClass = Part::FaceMakerBullseye
  LengthFwd = -1
  LengthRev = 0
  Solid = true
  Symmetric = false
FEATURE [Part::Extrusion] Extrude062
  Base = -> Face079
  Dir = (0,0,-1)
  DirMode = 2
  FaceMakerClass = Part::FaceMakerBullseye
  LengthFwd = 1
  LengthRev = 0
  Solid = true
  Symmetric = false
FEATURE [Part::Extrusion] Extrude063
  Base = -> Face080
  Dir = (0,0,-1)
  DirMode = 2
  FaceMakerClass = Part::FaceMakerBullseye
  LengthFwd = 1
  LengthRev = 0
  Solid = true
  Symmetric = false
FEATURE [Part::Extrusion] Extrude064
  Base = -> Cut027
  Dir = (0,0,1)
  DirMode = 2
  FaceMakerClass = Part::FaceMakerBullseye
  LengthFwd = -1
  LengthRev = 0
  Solid = true
  Symmetric = false
FEATURE [Part::Extrusion] Extrude065
  Base = -> Face083
  Dir = (0,0,-1)
  DirMode = 2
  FaceMakerClass = Part::FaceMakerBullseye
  LengthFwd = 1
  LengthRev = 0
  Solid = true
  Symmetric = false
FEATURE [Part::Extrusion] Extrude066
  Base = -> Face084
  Dir = (0,0,-1)
  DirMode = 2
  FaceMakerClass = Part::FaceMakerBullseye
  LengthFwd = 1
  LengthRev = 0
  Solid = true
  Symmetric = false
FEATURE [Part::Extrusion] Extrude067
  Base = -> Cut028
  Dir = (0,0,-1)
  DirMode = 2
  FaceMakerClass = Part::FaceMakerBullseye
  LengthFwd = 1
  LengthRev = 0
  Solid = true
  Symmetric = false
FEATURE [Part::Extrusion] Extrude068
  Base = -> Face087
  Dir = (0,0,-1)
  DirMode = 2
  FaceMakerClass = Part::FaceMakerBullseye
  LengthFwd = 1
  LengthRev = 0
  Solid = true
  Symmetric = false
FEATURE [Part::Extrusion] Extrude069
  Base = -> Face088
  Dir = (0,0,-1)
  DirMode = 2
  FaceMakerClass = Part::FaceMakerBullseye
  LengthFwd = 1
  LengthRev = 0
  Solid = true
  Symmetric = false
FEATURE [Part::Extrusion] Extrude070
  Base = -> Face089
  Dir = (0,0,-1)
  DirMode = 2
  FaceMakerClass = Part::FaceMakerBullseye
  LengthFwd = 1
  LengthRev = 0
  Solid = true
  Symmetric = false
FEATURE [Part::Extrusion] Extrude071
  Base = -> Cut029
  Dir = (0,0,-1)
  DirMode = 2
  FaceMakerClass = Part::FaceMakerBullseye
  LengthFwd = 1
  LengthRev = 0
  Solid = true
  Symmetric = false
FEATURE [Part::Extrusion] Extrude072
  Base = -> Face092
  Dir = (0,0,-1)
  DirMode = 2
  FaceMakerClass = Part::FaceMakerBullseye
  LengthFwd = 1
  LengthRev = 0
  Solid = true
  Symmetric = false
FEATURE [Part::Extrusion] Extrude073
  Base = -> Cut030
  Dir = (0,0,-1)
  DirMode = 2
  FaceMakerClass = Part::FaceMakerBullseye
  LengthFwd = 1
  LengthRev = 0
  Solid = true
  Symmetric = false
FEATURE [Part::Extrusion] Extrude074
  Base = -> Face095
  Dir = (0,0,-1)
  DirMode = 2
  FaceMakerClass = Part::FaceMakerBullseye
  LengthFwd = 1
  LengthRev = 0
  Solid = true
  Symmetric = false
FEATURE [Part::Extrusion] Extrude075
  Base = -> Cut031
  Dir = (0,0,-1)
  DirMode = 2
  FaceMakerClass = Part::FaceMakerBullseye
  LengthFwd = 1
  LengthRev = 0
  Solid = true
  Symmetric = false
FEATURE [Part::Extrusion] Extrude076
  Base = -> Face098
  Dir = (0,0,-1)
  DirMode = 2
  FaceMakerClass = Part::FaceMakerBullseye
  LengthFwd = 1
  LengthRev = 0
  Solid = true
  Symmetric = false
FEATURE [Part::MultiFuse] Fusion013  label="name"
  Placement = pos=(13,22,-6.5) rot=(0.707107,0.707107,0;3.14159rad)
  Shapes = -> [Extrude076,Extrude075,Extrude074,Extrude073,Extrude072,Extrude071,Extrude070,Extrude069,Extrude068,Extrude067,Extrude066,Extrude065,Extrude064,Extrude063,Extrude062,Extrude061,Extrude060]
FEATURE [Part::Feature] Face099
  shape: bbox 1.87 x 2.42 x 2e-07 mm, 1 faces, 0 solids (baked)
FEATURE [Part::Feature] Face100
  shape: bbox 0.2334 x 1.66 x 2e-07 mm, 1 faces, 0 solids (baked)
FEATURE [Part::Feature] Face101
  shape: bbox 0.2362 x 0.3326 x 2e-07 mm, 1 faces, 0 solids (baked)
FEATURE [Part::Feature] Face102
  shape: bbox 1.319 x 2.398 x 2e-07 mm, 1 faces, 0 solids (baked)
FEATURE [Part::Feature] Face103
  shape: bbox 0.8379 x 1.286 x 2e-07 mm, 1 faces, 0 solids (baked)
FEATURE [Part::Cut] Cut032
  Base = -> Face102
  Tool = -> Face103
FEATURE [Part::Feature] Face104
  shape: bbox 0.6692 x 0.2281 x 2e-07 mm, 1 faces, 0 solids (baked)
FEATURE [Part::Feature] Face105
  shape: bbox 1.87 x 2.42 x 2e-07 mm, 1 faces, 0 solids (baked)
FEATURE [Part::Feature] Face106
  shape: bbox 0.2334 x 1.66 x 2e-07 mm, 1 faces, 0 solids (baked)
FEATURE [Part::Feature] Face107
  shape: bbox 0.2362 x 0.3326 x 2e-07 mm, 1 faces, 0 solids (baked)
FEATURE [Part::Feature] Face108
  shape: bbox 1.319 x 2.398 x 2e-07 mm, 1 faces, 0 solids (baked)
FEATURE [Part::Feature] Face109
  shape: bbox 0.8379 x 1.286 x 2e-07 mm, 1 faces, 0 solids (baked)
FEATURE [Part::Cut] Cut033
  Base = -> Face108
  Tool = -> Face109
FEATURE [Part::Feature] Face110
  shape: bbox 1.386 x 1.78 x 2e-07 mm, 1 faces, 0 solids (baked)
FEATURE [Part::Feature] Face111
  shape: bbox 0.731 x 0.6621 x 2e-07 mm, 1 faces, 0 solids (baked)
FEATURE [Part::Cut] Cut034
  Base = -> Face110
  Tool = -> Face111
FEATURE [Part::Feature] Face112
  shape: bbox 0.6748 x 2.189 x 2e-07 mm, 1 faces, 0 solids (baked)
FEATURE [Part::Feature] Face113
  shape: bbox 1.788 x 2.309 x 2e-07 mm, 1 faces, 0 solids (baked)
FEATURE [Part::Feature] Face114
  shape: bbox 0.6523 x 1.052 x 2e-07 mm, 1 faces, 0 solids (baked)
FEATURE [Part::Cut] Cut035
  Base = -> Face113
  Tool = -> Face114
FEATURE [Part::Feature] Face115
  shape: bbox 0.6748 x 2.189 x 2e-07 mm, 1 faces, 0 solids (baked)
FEATURE [Part::Feature] Face116
  shape: bbox 1.386 x 1.78 x 2e-07 mm, 1 faces, 0 solids (baked)
FEATURE [Part::Feature] Face117
  shape: bbox 0.731 x 0.6621 x 2e-07 mm, 1 faces, 0 solids (baked)
FEATURE [Part::Cut] Cut036
  Base = -> Face116
  Tool = -> Face117
FEATURE [Part::Feature] Face118
  shape: bbox 0.7085 x 1.707 x 2e-07 mm, 1 faces, 0 solids (baked)
FEATURE [Part::Feature] Face119
  shape: bbox 0.2334 x 1.66 x 2e-07 mm, 1 faces, 0 solids (baked)
FEATURE [Part::Feature] Face120
  shape: bbox 0.2362 x 0.3326 x 2e-07 mm, 1 faces, 0 solids (baked)
FEATURE [Part::Feature] Face121
  shape: bbox 1.788 x 2.309 x 2e-07 mm, 1 faces, 0 solids (baked)
FEATURE [Part::Feature] Face122
  shape: bbox 0.6523 x 1.052 x 2e-07 mm, 1 faces, 0 solids (baked)
FEATURE [Part::Cut] Cut037
  Base = -> Face121
  Tool = -> Face122
FEATURE [Part::Feature] Face123
  shape: bbox 1.293 x 2.398 x 2e-07 mm, 1 faces, 0 solids (baked)
FEATURE [Part::Feature] Face124
  shape: bbox 0.8098 x 1.293 x 2e-07 mm, 1 faces, 0 solids (baked)
FEATURE [Part::Cut] Cut038
  Base = -> Face123
  Tool = -> Face124
FEATURE [Part::Feature] Face125
  shape: bbox 1.33 x 1.78 x 2e-07 mm, 1 faces, 0 solids (baked)
FEATURE [Part::Feature] Face126
  shape: bbox 0.8295 x 0.5069 x 2e-07 mm, 1 faces, 0 solids (baked)
FEATURE [Part::Cut] Cut039
  Base = -> Face125
  Tool = -> Face126
FEATURE [Part::Feature] Face127
  shape: bbox 1.13 x 1.774 x 2e-07 mm, 1 faces, 0 solids (baked)
FEATURE [Part::Feature] Face128
  shape: bbox 1.111 x 2.275 x 2e-07 mm, 1 faces, 0 solids (baked)
FEATURE [Part::Feature] Face129
  shape: bbox 1.757 x 1.73 x 2e-07 mm, 1 faces, 0 solids (baked)
FEATURE [Part::Feature] Face130
  shape: bbox 0.3205 x 1.685 x 2e-07 mm, 1 faces, 0 solids (baked)
FEATURE [Part::Feature] Face131
  shape: bbox 0.3205 x 0.4118 x 2e-07 mm, 1 faces, 0 solids (baked)
FEATURE [Part::Feature] Face132
  shape: bbox 0.6889 x 2.161 x 2e-07 mm, 1 faces, 0 solids (baked)
FEATURE [Part::Feature] Face133
  shape: bbox 1.111 x 2.275 x 2e-07 mm, 1 faces, 0 solids (baked)
FEATURE [Part::Feature] Face134
  shape: bbox 1.192 x 2.319 x 2e-07 mm, 1 faces, 0 solids (baked)
FEATURE [Part::Feature] Face135
  shape: bbox 0.5511 x 1.023 x 2e-07 mm, 1 faces, 0 solids (baked)
FEATURE [Part::Cut] Cut040
  Base = -> Face134
  Tool = -> Face135
FEATURE [Part::Feature] Face136
  shape: bbox 0.3205 x 1.685 x 2e-07 mm, 1 faces, 0 solids (baked)
FEATURE [Part::Feature] Face137
  shape: bbox 0.3205 x 0.4118 x 2e-07 mm, 1 faces, 0 solids (baked)
FEATURE [Part::Feature] Face138
  shape: bbox 1.063 x 1.685 x 2e-07 mm, 1 faces, 0 solids (baked)
FEATURE [Part::Feature] Face139
  shape: bbox 1.701 x 2.395 x 2e-07 mm, 1 faces, 0 solids (baked)
FEATURE [Part::Feature] Face140
  shape: bbox 0.4555 x 0.7096 x 2e-07 mm, 1 faces, 0 solids (baked)
FEATURE [Part::Cut] Cut041
  Base = -> Face139
  Tool = -> Face140
FEATURE [Part::Feature] Face141
  shape: bbox 1.181 x 2.417 x 2e-07 mm, 1 faces, 0 solids (baked)
FEATURE [Part::Feature] Face142
  shape: bbox 0.5286 x 0.9789 x 2e-07 mm, 1 faces, 0 solids (baked)
FEATURE [Part::Cut] Cut042
  Base = -> Face141
  Tool = -> Face142
FEATURE [Part::Feature] Face143
  shape: bbox 1.757 x 1.73 x 2e-07 mm, 1 faces, 0 solids (baked)
FEATURE [Part::Feature] Face144
  shape: bbox 1.147 x 1.774 x 2e-07 mm, 1 faces, 0 solids (baked)
FEATURE [Part::Feature] Face145
  shape: bbox 0.4386 x 0.548 x 2e-07 mm, 1 faces, 0 solids (baked)
FEATURE [Part::Cut] Cut043
  Base = -> Face144
  Tool = -> Face145
FEATURE [Part::Feature] Face146
  shape: bbox 0.3205 x 0.4118 x 2e-07 mm, 1 faces, 0 solids (baked)
FEATURE [Part::Feature] Face147
  shape: bbox 0.3205 x 1.685 x 2e-07 mm, 1 faces, 0 solids (baked)
FEATURE [Part::Feature] Face148
  shape: bbox 0.3205 x 2.275 x 2e-07 mm, 1 faces, 0 solids (baked)
FEATURE [Part::Feature] Face149
  shape: bbox 0.3458 x 0.4657 x 2e-07 mm, 1 faces, 0 solids (baked)
FEATURE [Part::Feature] Face150
  shape: bbox 1.13 x 1.774 x 2e-07 mm, 1 faces, 0 solids (baked)
FEATURE [Part::Feature] Face151
  shape: bbox 1.254 x 1.774 x 2e-07 mm, 1 faces, 0 solids (baked)
FEATURE [Part::Feature] Face152
  shape: bbox 0.5905 x 1.026 x 2e-07 mm, 1 faces, 0 solids (baked)
FEATURE [Part::Cut] Cut044
  Base = -> Face151
  Tool = -> Face152
FEATURE [Part::Feature] Face153
  shape: bbox 1.757 x 1.73 x 2e-07 mm, 1 faces, 0 solids (baked)
FEATURE [Part::Extrusion] Extrude077
  Base = -> Face099
  Dir = (0,0,-1)
  DirMode = 2
  FaceMakerClass = Part::FaceMakerBullseye
  LengthFwd = 1
  LengthRev = 0
  Solid = true
  Symmetric = false
FEATURE [Part::Extrusion] Extrude078
  Base = -> Face100
  Dir = (0,0,-1)
  DirMode = 2
  FaceMakerClass = Part::FaceMakerBullseye
  LengthFwd = 1
  LengthRev = 0
  Solid = true
  Symmetric = false
FEATURE [Part::Extrusion] Extrude079
  Base = -> Face101
  Dir = (0,0,-1)
  DirMode = 2
  FaceMakerClass = Part::FaceMakerBullseye
  LengthFwd = 1
  LengthRev = 0
  Solid = true
  Symmetric = false
FEATURE [Part::Extrusion] Extrude080
  Base = -> Cut032
  Dir = (0,0,-1)
  DirMode = 2
  FaceMakerClass = Part::FaceMakerBullseye
  LengthFwd = 1
  LengthRev = 0
  Solid = true
  Symmetric = false
FEATURE [Part::Extrusion] Extrude081
  Base = -> Face104
  Dir = (0,0,-1)
  DirMode = 2
  FaceMakerClass = Part::FaceMakerBullseye
  LengthFwd = 1
  LengthRev = 0
  Solid = true
  Symmetric = false
FEATURE [Part::Extrusion] Extrude082
  Base = -> Face105
  Dir = (0,0,-1)
  DirMode = 2
  FaceMakerClass = Part::FaceMakerBullseye
  LengthFwd = 1
  LengthRev = 0
  Solid = true
  Symmetric = false
FEATURE [Part::Extrusion] Extrude083
  Base = -> Face106
  Dir = (0,0,-1)
  DirMode = 2
  FaceMakerClass = Part::FaceMakerBullseye
  LengthFwd = 1
  LengthRev = 0
  Solid = true
  Symmetric = false
FEATURE [Part::Extrusion] Extrude084
  Base = -> Face107
  Dir = (0,0,-1)
  DirMode = 2
  FaceMakerClass = Part::FaceMakerBullseye
  LengthFwd = 1
  LengthRev = 0
  Solid = true
  Symmetric = false
FEATURE [Part::Extrusion] Extrude085
  Base = -> Cut033
  Dir = (0,0,-1)
  DirMode = 2
  FaceMakerClass = Part::FaceMakerBullseye
  LengthFwd = 1
  LengthRev = 0
  Solid = true
  Symmetric = false
FEATURE [Part::Extrusion] Extrude086
  Base = -> Cut034
  Dir = (0,0,1)
  DirMode = 2
  FaceMakerClass = Part::FaceMakerBullseye
  LengthFwd = -1
  LengthRev = 0
  Solid = true
  Symmetric = false
FEATURE [Part::Extrusion] Extrude087
  Base = -> Face112
  Dir = (0,0,1)
  DirMode = 2
  FaceMakerClass = Part::FaceMakerBullseye
  LengthFwd = -1
  LengthRev = 0
  Solid = true
  Symmetric = false
FEATURE [Part::Extrusion] Extrude088
  Base = -> Cut035
  Dir = (0,0,-1)
  DirMode = 2
  FaceMakerClass = Part::FaceMakerBullseye
  LengthFwd = 1
  LengthRev = 0
  Solid = true
  Symmetric = false
FEATURE [Part::Extrusion] Extrude089
  Base = -> Face115
  Dir = (0,0,1)
  DirMode = 2
  FaceMakerClass = Part::FaceMakerBullseye
  LengthFwd = -1
  LengthRev = 0
  Solid = true
  Symmetric = false
FEATURE [Part::Extrusion] Extrude090
  Base = -> Cut036
  Dir = (0,0,1)
  DirMode = 2
  FaceMakerClass = Part::FaceMakerBullseye
  LengthFwd = -1
  LengthRev = 0
  Solid = true
  Symmetric = false
FEATURE [Part::Extrusion] Extrude091
  Base = -> Face118
  Dir = (0,0,-1)
  DirMode = 2
  FaceMakerClass = Part::FaceMakerBullseye
  LengthFwd = 1
  LengthRev = 0
  Solid = true
  Symmetric = false
FEATURE [Part::Extrusion] Extrude092
  Base = -> Face119
  Dir = (0,0,-1)
  DirMode = 2
  FaceMakerClass = Part::FaceMakerBullseye
  LengthFwd = 1
  LengthRev = 0
  Solid = true
  Symmetric = false
FEATURE [Part::Extrusion] Extrude093
  Base = -> Face120
  Dir = (0,0,-1)
  DirMode = 2
  FaceMakerClass = Part::FaceMakerBullseye
  LengthFwd = 1
  LengthRev = 0
  Solid = true
  Symmetric = false
FEATURE [Part::Extrusion] Extrude094
  Base = -> Cut037
  Dir = (0,0,-1)
  DirMode = 2
  FaceMakerClass = Part::FaceMakerBullseye
  LengthFwd = 1
  LengthRev = 0
  Solid = true
  Symmetric = false
FEATURE [Part::Extrusion] Extrude095
  Base = -> Cut038
  Dir = (0,0,1)
  DirMode = 2
  FaceMakerClass = Part::FaceMakerBullseye
  LengthFwd = -1
  LengthRev = 0
  Solid = true
  Symmetric = false
FEATURE [Part::Extrusion] Extrude096
  Base = -> Cut039
  Dir = (0,0,-1)
  DirMode = 2
  FaceMakerClass = Part::FaceMakerBullseye
  LengthFwd = 1
  LengthRev = 0
  Solid = true
  Symmetric = false
FEATURE [Part::Extrusion] Extrude097
  Base = -> Face127
  Dir = (0,0,1)
  DirMode = 2
  FaceMakerClass = Part::FaceMakerBullseye
  LengthFwd = -1
  LengthRev = 0
  Solid = true
  Symmetric = false
FEATURE [Part::Extrusion] Extrude098
  Base = -> Face128
  Dir = (0,0,-1)
  DirMode = 2
  FaceMakerClass = Part::FaceMakerBullseye
  LengthFwd = 1
  LengthRev = 0
  Solid = true
  Symmetric = false
FEATURE [Part::Extrusion] Extrude099
  Base = -> Face129
  Dir = (0,0,-1)
  DirMode = 2
  FaceMakerClass = Part::FaceMakerBullseye
  LengthFwd = 1
  LengthRev = 0
  Solid = true
  Symmetric = false
FEATURE [Part::Extrusion] Extrude100
  Base = -> Face130
  Dir = (0,0,-1)
  DirMode = 2
  FaceMakerClass = Part::FaceMakerBullseye
  LengthFwd = 1
  LengthRev = 0
  Solid = true
  Symmetric = false
FEATURE [Part::Extrusion] Extrude101
  Base = -> Face131
  Dir = (0,0,-1)
  DirMode = 2
  FaceMakerClass = Part::FaceMakerBullseye
  LengthFwd = 1
  LengthRev = 0
  Solid = true
  Symmetric = false
FEATURE [Part::Extrusion] Extrude102
  Base = -> Face132
  Dir = (0,0,-1)
  DirMode = 2
  FaceMakerClass = Part::FaceMakerBullseye
  LengthFwd = 1
  LengthRev = 0
  Solid = true
  Symmetric = false
FEATURE [Part::Extrusion] Extrude103
  Base = -> Face133
  Dir = (0,0,-1)
  DirMode = 2
  FaceMakerClass = Part::FaceMakerBullseye
  LengthFwd = 1
  LengthRev = 0
  Solid = true
  Symmetric = false
FEATURE [Part::Extrusion] Extrude104
  Base = -> Cut040
  Dir = (0,0,-1)
  DirMode = 2
  FaceMakerClass = Part::FaceMakerBullseye
  LengthFwd = 1
  LengthRev = 0
  Solid = true
  Symmetric = false
FEATURE [Part::Extrusion] Extrude105
  Base = -> Face136
  Dir = (0,0,-1)
  DirMode = 2
  FaceMakerClass = Part::FaceMakerBullseye
  LengthFwd = 1
  LengthRev = 0
  Solid = true
  Symmetric = false
FEATURE [Part::Extrusion] Extrude106
  Base = -> Face137
  Dir = (0,0,-1)
  DirMode = 2
  FaceMakerClass = Part::FaceMakerBullseye
  LengthFwd = 1
  LengthRev = 0
  Solid = true
  Symmetric = false
FEATURE [Part::Extrusion] Extrude107
  Base = -> Face138
  Dir = (0,0,-1)
  DirMode = 2
  FaceMakerClass = Part::FaceMakerBullseye
  LengthFwd = 1
  LengthRev = 0
  Solid = true
  Symmetric = false
FEATURE [Part::Extrusion] Extrude108
  Base = -> Cut041
  Dir = (0,0,-1)
  DirMode = 2
  FaceMakerClass = Part::FaceMakerBullseye
  LengthFwd = 1
  LengthRev = 0
  Solid = true
  Symmetric = false
FEATURE [Part::Extrusion] Extrude109
  Base = -> Cut042
  Dir = (0,0,1)
  DirMode = 2
  FaceMakerClass = Part::FaceMakerBullseye
  LengthFwd = -1
  LengthRev = 0
  Solid = true
  Symmetric = false
FEATURE [Part::Extrusion] Extrude110
  Base = -> Cut043
  Dir = (0,0,1)
  DirMode = 2
  FaceMakerClass = Part::FaceMakerBullseye
  LengthFwd = -1
  LengthRev = 0
  Solid = true
  Symmetric = false
FEATURE [Part::Extrusion] Extrude111
  Base = -> Face143
  Dir = (0,0,-1)
  DirMode = 2
  FaceMakerClass = Part::FaceMakerBullseye
  LengthFwd = 1
  LengthRev = 0
  Solid = true
  Symmetric = false
FEATURE [Part::Extrusion] Extrude112
  Base = -> Face146
  Dir = (0,0,-1)
  DirMode = 2
  FaceMakerClass = Part::FaceMakerBullseye
  LengthFwd = 1
  LengthRev = 0
  Solid = true
  Symmetric = false
FEATURE [Part::Extrusion] Extrude113
  Base = -> Face147
  Dir = (0,0,-1)
  DirMode = 2
  FaceMakerClass = Part::FaceMakerBullseye
  LengthFwd = 1
  LengthRev = 0
  Solid = true
  Symmetric = false
FEATURE [Part::Extrusion] Extrude114
  Base = -> Face148
  Dir = (0,0,-1)
  DirMode = 2
  FaceMakerClass = Part::FaceMakerBullseye
  LengthFwd = 1
  LengthRev = 0
  Solid = true
  Symmetric = false
FEATURE [Part::Extrusion] Extrude115
  Base = -> Face149
  Dir = (0,0,-1)
  DirMode = 2
  FaceMakerClass = Part::FaceMakerBullseye
  LengthFwd = 1
  LengthRev = 0
  Solid = true
  Symmetric = false
FEATURE [Part::Extrusion] Extrude116
  Base = -> Cut044
  Dir = (0,0,-1)
  DirMode = 2
  FaceMakerClass = Part::FaceMakerBullseye
  LengthFwd = 1
  LengthRev = 0
  Solid = true
  Symmetric = false
FEATURE [Part::Extrusion] Extrude117
  Base = -> Face153
  Dir = (0,0,-1)
  DirMode = 2
  FaceMakerClass = Part::FaceMakerBullseye
  LengthFwd = 1
  LengthRev = 0
  Solid = true
  Symmetric = false
FEATURE [Part::Extrusion] Extrude118
  Base = -> Face150
  Dir = (0,0,1)
  DirMode = 2
  FaceMakerClass = Part::FaceMakerBullseye
  LengthFwd = -1
  LengthRev = 0
  Solid = true
  Symmetric = false
FEATURE [Part::MultiFuse] Fusion014  label="contact"
  Placement = pos=(13,52,-6.5) rot=(0.707107,0.707107,0;3.14159rad)
  Shapes = -> [Extrude095,Extrude092,Extrude094,Extrude105,Extrude080,Extrude110,Extrude077,Extrude101,Extrude103,Extrude081,Extrude106,Extrude086,Extrude089,Extrude109,Extrude085,Extrude104,Extrude078,Extrude087,Extrude113,Extrude118,Extrude115,Extrude116,Extrude107,Extrude102,Extrude084,Extrude099,Extrude111,Extrude091,Extrude108,Extrude079,Extrude100,Extrude112,Extrude097,Extrude117,Extrude083,Extrude098,+6 more]
FEATURE [Part::Fillet] Fillet007
  Base = -> Box009
  Edges = 4 edges r=1: [Edge1,Edge3,Edge5,Edge7]
  Placement = pos=(0,0,1) rot=(0,0,1;0rad)
FEATURE [Part::Chamfer] Chamfer001  label="top_w_guides"
  Base = -> Cut007
  Edges = 5 edges r=1: [Edge131,Edge133,Edge135,Edge137,Edge138]
FEATURE [App::DocumentObjectGroup] Group001  label="cart_top"
  Group = -> [Box006,Box007,Chamfer,Fillet001,Fusion003,Fillet002,Cut007,Chamfer001]
FEATURE [Part::Chamfer] Chamfer002  label="bottom_w_guides"
  Base = -> Cut012
  Edges = 5 edges r=1: [Edge2,Edge3,Edge4,Edge5,Edge6]
FEATURE [App::DocumentObjectGroup] Group002  label="cart_bottom"
  Group = -> [Box008,Solid001,Fusion005,Cut012,Chamfer002]
